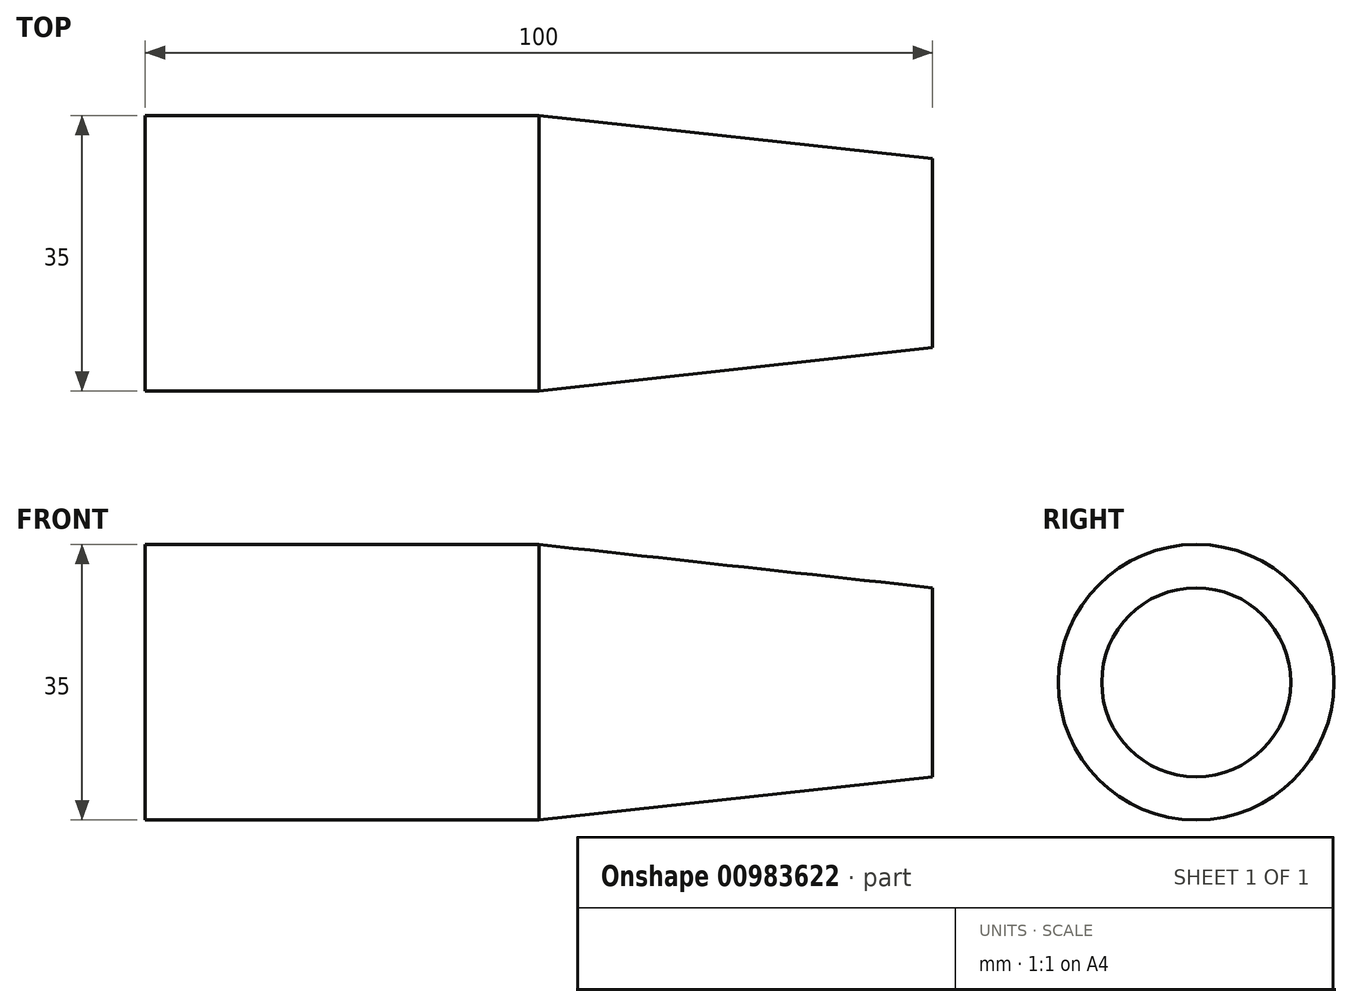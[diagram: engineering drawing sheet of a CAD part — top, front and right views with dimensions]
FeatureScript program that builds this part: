
annotation { "Feature Type Name" : "Feature", "Feature Type Description" : "" }
export const myFeature = defineFeature(function(context is Context, id is Id, definition is map)
    precondition{}
    {
        {
            var Q0;
            Q0=qCreatedBy(makeId("Top.planeOp"),FACE);
            var sketch = newSketch(context, id + "F0", { "sketchPlane" : qUnion([Q0])});
            skLineSegment(sketch, "E0", {"start": v(0, 0) * mm, "end": v(100, 0) * mm});
            skLineSegment(sketch, "E1", {"start": v(100, 0) * mm, "end": v(100, 12) * mm});
            skLineSegment(sketch, "E2", {"start": v(100, 0) * mm, "end": v(50, 0) * mm});
            skLineSegment(sketch, "E3", {"start": v(50, 17.5) * mm, "end": v(100, 12) * mm});
            skLineSegment(sketch, "E4", {"start": v(50, 17.5) * mm, "end": v(0, 17.5) * mm});
            skLineSegment(sketch, "E5", {"start": v(0, 17.5) * mm, "end": v(0, 0) * mm});
            skSolve(sketch);
        }
        {
            var Q0;
            Q0=makeQuery(id+"F0.imprint","IMPRINT",FACE,{"disambiguationData":[TD([[makeQuery(id+"F0.imprint","IMPRINT",EDGE,{"derivedFrom":sQuery(id+"F0.wireOp",EDGE,"E0")}),1.0]])]});
            var Q1;
            Q1=makeQuery(id+"F0.imprint","IMPRINT",FACE,{"disambiguationData":[TD([[makeQuery(id+"F0.imprint","IMPRINT",EDGE,{"derivedFrom":sQuery(id+"F0.wireOp",EDGE,"E0")}),1.0]])]});
            var Q2;
            Q2=makeQuery(id+"F0.imprint","IMPRINT",FACE,{"disambiguationData":[TD([[makeQuery(id+"F0.imprint","IMPRINT",EDGE,{"derivedFrom":sQuery(id+"F0.wireOp",EDGE,"E0")}),1.0]])]});
            var Q3;
            Q3=sQuery(id+"F0.wireOp",EDGE,"E0");
            revolve(context, id + "F1", {"surfaceOperationType" : NewSurfaceOperationType.NEW, "entities" : qUnion([Q0, Q1, Q2]), "axis" : qUnion([Q3]), "revolveType" : RevolveType.FULL});
        }
    });
